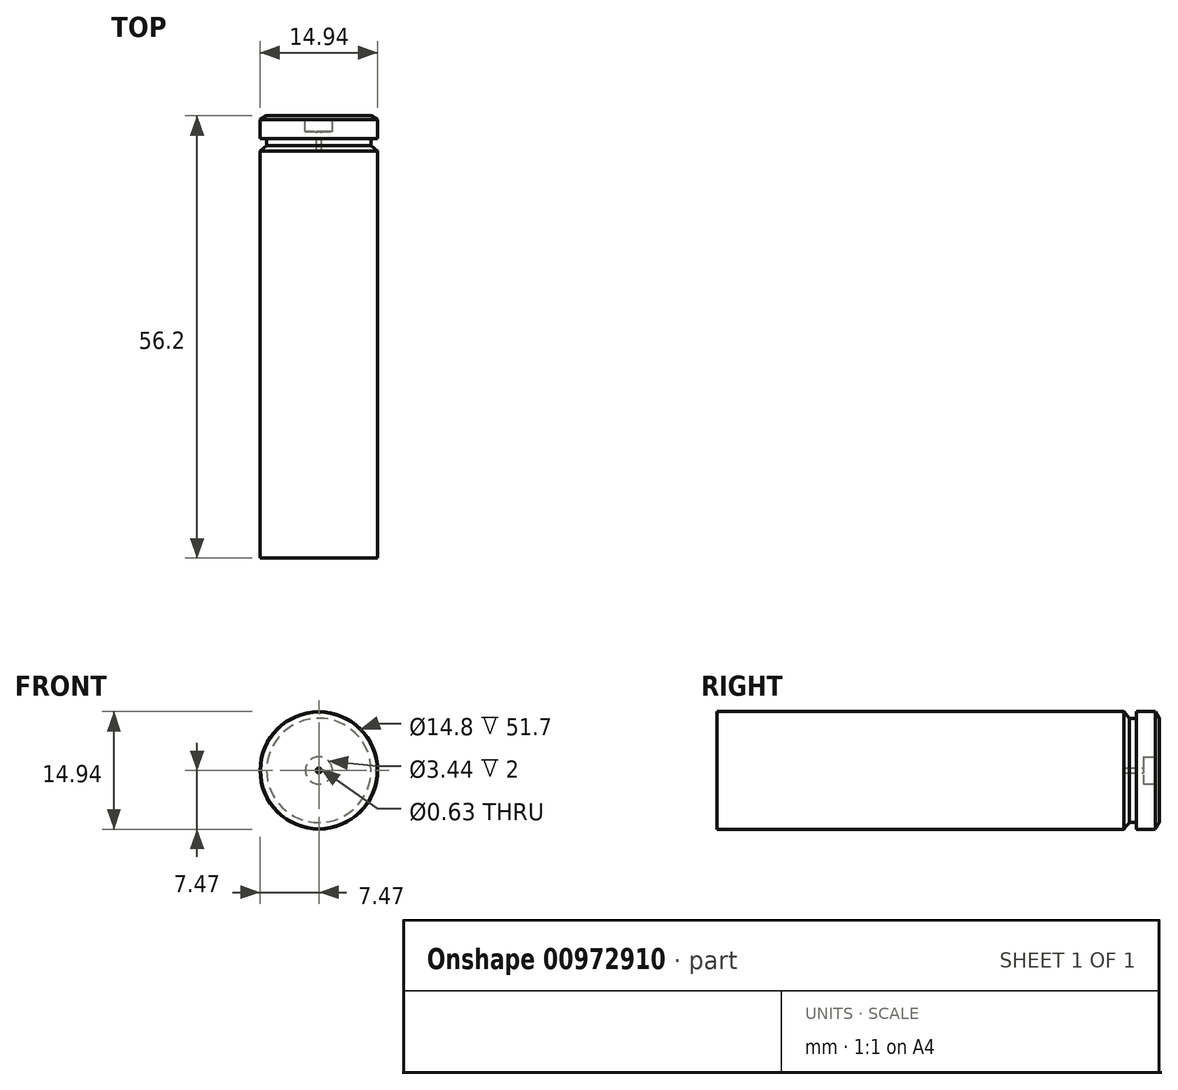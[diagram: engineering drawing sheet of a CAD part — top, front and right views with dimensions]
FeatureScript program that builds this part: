
annotation { "Feature Type Name" : "Feature", "Feature Type Description" : "" }
export const myFeature = defineFeature(function(context is Context, id is Id, definition is map)
    precondition{}
    {
        {
            var Q0;
            Q0=qCreatedBy(makeId("Right.planeOp"),FACE);
            var sketch = newSketch(context, id + "F0", { "sketchPlane" : qUnion([Q0])});
            skLineSegment(sketch, "E0", {"start": v(0, 0) * mm, "end": v(0, 6.62) * mm});
            skLineSegment(sketch, "E1", {"start": v(0, 6.62) * mm, "end": v(-0.5, 7.46) * mm});
            skLineSegment(sketch, "E2", {"start": v(-0.5, 7.47) * mm, "end": v(-2.9, 7.47) * mm});
            skLineSegment(sketch, "E3", {"start": v(-2.9, 7.46) * mm, "end": v(-2.9, 6.62) * mm});
            skLineSegment(sketch, "E4", {"start": v(-2.9, 6.62) * mm, "end": v(-3.8, 6.62) * mm});
            skLineSegment(sketch, "E5", {"start": v(-3.8, 6.62) * mm, "end": v(-4.5, 7.47) * mm});
            skLineSegment(sketch, "E6", {"start": v(-4.5, 7.46) * mm, "end": v(-4.5, 0) * mm});
            skLineSegment(sketch, "E7", {"start": v(-4.5, 0) * mm, "end": v(0, 0) * mm});
            skSolve(sketch);
        }
        {
            var Q0;
            Q0 = qSketchRegion(id + "F0", true);
            var Q1;
            Q1=sQuery(id+"F0.wireOp",EDGE,"E7");
            revolve(context, id + "F1", {"surfaceOperationType" : NewSurfaceOperationType.NEW, "entities" : qUnion([Q0]), "axis" : qUnion([Q1]), "revolveType" : RevolveType.FULL});
        }
        {
            var Q0;
            Q0=makeQuery(id+"F1.opRevolve","SWEPT_FACE",FACE,{"disambiguationData":[OSD([sQuery(id+"F0.wireOp",EDGE,"E6")])]});
            var sketch = newSketch(context, id + "F2", { "sketchPlane" : qUnion([Q0])});
            skCircle(sketch, "E8", {"center": v(0, 0) * mm, "radius": 7.46 * mm});
            skCircle(sketch, "E9", {"center": v(0, 0) * mm, "radius": 7.4 * mm});
            skSolve(sketch);
        }
        {
            var Q0;
            Q0 = qSketchRegion(id + "F2", true);
            extrude(context, id + "F3", {"entities" : qUnion([Q0]), "operationType" : NewBodyOperationType.ADD, "depth" : 51.7 * mm, "offsetDistance" : 25 * mm});
        }
        {
            var Q0;
            Q0=makeQuery(id+"F1.opRevolve","SWEPT_FACE",FACE,{"disambiguationData":[OSD([sQuery(id+"F0.wireOp",EDGE,"E0")])]});
            var sketch = newSketch(context, id + "F4", { "sketchPlane" : qUnion([Q0])});
            skCircle(sketch, "E10", {"center": v(0, 0) * mm, "radius": 1.72 * mm});
            skSolve(sketch);
        }
        {
            var Q0;
            Q0 = qSketchRegion(id + "F4", true);
            extrude(context, id + "F5", {"entities" : qUnion([Q0]), "operationType" : NewBodyOperationType.REMOVE, "oppositeDirection" : true, "depth" : 2 * mm, "offsetDistance" : 25 * mm});
        }
        {
            var Q0;
            Q0=makeQuery(id+"F5.boolean.opBoolean","COPY",FACE,{"derivedFrom":makeQuery(id+"F5.opExtrude","CAP_FACE",FACE,{"disambiguationData":[OSD([sQuery(id+"F4.wireOp",EDGE,"E10")])],"isStart":false})});
            var sketch = newSketch(context, id + "F6", { "sketchPlane" : qUnion([Q0])});
            skCircle(sketch, "E11", {"center": v(0, 0) * mm, "radius": 0.31 * mm});
            skSolve(sketch);
        }
        {
            var Q0;
            Q0=makeQuery(id+"F6.imprint","IMPRINT",FACE,{"disambiguationData":[TD([[makeQuery(id+"F6.imprint","IMPRINT",EDGE,{"derivedFrom":sQuery(id+"F6.wireOp",EDGE,"E11")}),1.0]])]});
            var Q1;
            Q1=sQuery(id+"F6.wireOp",EDGE,"E11");
            extrude(context, id + "F7", {"entities" : qUnion([Q0]), "operationType" : NewBodyOperationType.REMOVE, "surfaceEntities" : qUnion([Q1]), "endBound" : BoundingType.THROUGH_ALL, "oppositeDirection" : true, "depth" : 25 * mm, "offsetDistance" : 25 * mm});
        }
    });
